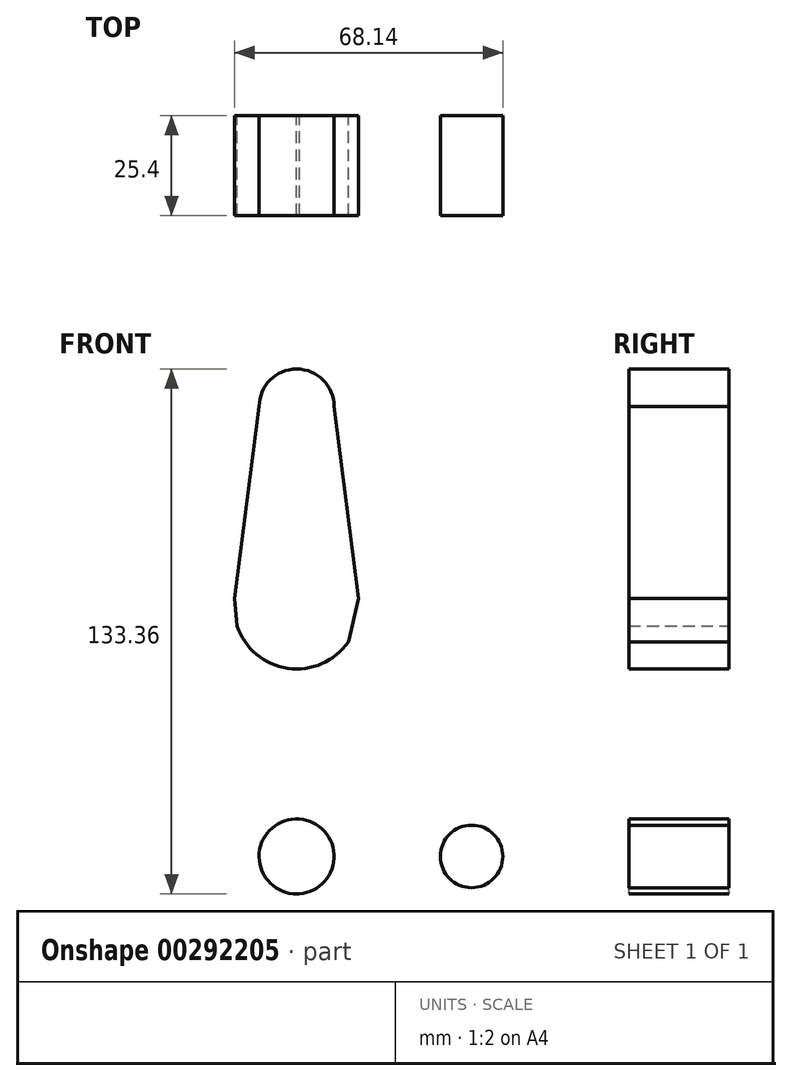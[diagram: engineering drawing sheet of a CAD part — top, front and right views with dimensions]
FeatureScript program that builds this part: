
annotation { "Feature Type Name" : "Feature", "Feature Type Description" : "" }
export const myFeature = defineFeature(function(context is Context, id is Id, definition is map)
    precondition{}
    {
        {
            var Q0;
            Q0=qCreatedBy(makeId("Front.planeOp"),FACE);
            var sketch = newSketch(context, id + "F0", { "sketchPlane" : qUnion([Q0])});
            skCircle(sketch, "E0", {"center": v(0, 114.3) * mm, "radius": 9.53 * mm});
            skCircle(sketch, "E1", {"center": v(0, 63.5) * mm, "radius": 15.88 * mm});
            skCircle(sketch, "E2", {"center": v(0, 0) * mm, "radius": 9.53 * mm});
            skCircle(sketch, "E3", {"center": v(44.45, 0) * mm, "radius": 7.94 * mm});
            skLineSegment(sketch, "E4", {"start": v(0, 114.3) * mm, "end": v(0, 79.38) * mm});
            skLineSegment(sketch, "E5", {"start": v(0, 0) * mm, "end": v(9.53, 0) * mm});
            skLineSegment(sketch, "E6.trimOffspring", {"start": v(0, 9.53) * mm, "end": v(0, 0) * mm});
            skPoint(sketch, "E7.start.orphan", {"position": v(-9.53, 114.3) * mm});
            skLineSegment(sketch, "E8", {"start": v(-9.53, 114.3) * mm, "end": v(-15.75, 65.5) * mm});
            skLineSegment(sketch, "E9", {"start": v(-15.75, 65.5) * mm, "end": v(-9.57, 0) * mm});
            skLineSegment(sketch, "E10.trimOffspring", {"start": v(36.51, 0) * mm, "end": v(44.45, 0) * mm});
            skLineSegment(sketch, "E11", {"start": v(18.97, 8.85) * mm, "end": v(44.73, 7.93) * mm});
            skLineSegment(sketch, "E12", {"start": v(0, -9.53) * mm, "end": v(44.73, -7.93) * mm});
            skPoint(sketch, "E13.end.orphan", {"position": v(234.08, -36.82) * mm});
            skArc(sketch, "E14.filletArc", {"start": v(11.34, 17.61) * mm, "mid": v(13.25, 11.58) * mm, "end": v(18.97, 8.85) * mm});
            skLineSegment(sketch, "E15", {"start": v(9.52, 114.3) * mm, "end": v(15.75, 65.5) * mm});
            skLineSegment(sketch, "E16", {"start": v(15.75, 65.5) * mm, "end": v(13.11, 54.55) * mm});
            skLineSegment(sketch, "E17", {"start": v(1.66, -0.4) * mm, "end": v(9.53, 0) * mm});
            skLineSegment(sketch, "E18.trimOffspring", {"start": v(2.23, 9.26) * mm, "end": v(0, 0) * mm});
            skLineSegment(sketch, "E19", {"start": v(13.11, 54.55) * mm, "end": v(11.34, 17.61) * mm});
            skSolve(sketch);
        }
        {
            var Q0;
            {var subQ0=sQuery(id+"F0.wireOp",EDGE,"52DSyJSs-urWb-Q2Su-mGJg-sDY8tmNg4yd1");var subQ1=sQuery(id+"F0.wireOp",EDGE,"E0");var subQ2=makeQuery(id+"F0.imprint","INTERSECT",VERTEX,{"derivedFrom":[subQ1,subQ0]});Q0=makeQuery(id+"F0.imprint","IMPRINT",FACE,{"disambiguationData":[TD([[makeQuery(id+"F0.imprint","IMPRINT",EDGE,{"disambiguationData":[TD([[subQ2,1.0]])],"derivedFrom":subQ1}),-1.0]])]});}
            var Q1;
            {var subQ0=sQuery(id+"F0.wireOp",EDGE,"E8");Q1=makeQuery(id+"F0.imprint","IMPRINT",FACE,{"disambiguationData":[TD([[makeQuery(id+"F0.imprint","IMPRINT",EDGE,{"derivedFrom":subQ0}),1.0]])]});}
            var Q2;
            {var subQ0=sQuery(id+"F0.wireOp",EDGE,"E0");var subQ1=makeQuery(id+"F0.imprint","INTERSECT",VERTEX,{"derivedFrom":[subQ0,sQuery(id+"F0.wireOp",EDGE,"E8")]});Q2=makeQuery(id+"F0.imprint","IMPRINT",FACE,{"disambiguationData":[TD([[makeQuery(id+"F0.imprint","IMPRINT",EDGE,{"disambiguationData":[TD([[subQ1,1.0]])],"derivedFrom":subQ0}),1.0]])]});}
            var Q3;
            {var subQ0=sQuery(id+"F0.wireOp",EDGE,"E1");var subQ1=makeQuery(id+"F0.imprint","INTERSECT",VERTEX,{"derivedFrom":[subQ0,sQuery(id+"F0.wireOp",EDGE,"E4")]});Q3=makeQuery(id+"F0.imprint","IMPRINT",FACE,{"disambiguationData":[TD([[makeQuery(id+"F0.imprint","IMPRINT",EDGE,{"disambiguationData":[TD([[subQ1,1.0]])],"derivedFrom":subQ0}),1.0]])]});}
            var Q4;
            {var subQ1=sQuery(id+"F0.wireOp",EDGE,"E5");Q4=makeQuery(id+"F0.imprint","IMPRINT",FACE,{"disambiguationData":[TD([[makeQuery(id+"F0.imprint","IMPRINT",EDGE,{"derivedFrom":subQ1}),-1.0]])]});}
            var Q5;
            {var subQ0=sQuery(id+"F0.wireOp",EDGE,"E3");var subQ1=makeQuery(id+"F0.imprint","IMPRINT",VERTEX,{"disambiguationData":[OD(0.0)],"derivedFrom":subQ0});Q5=makeQuery(id+"F0.imprint","IMPRINT",FACE,{"disambiguationData":[TD([[makeQuery(id+"F0.imprint","IMPRINT",EDGE,{"disambiguationData":[TD([[subQ1,1.0]])],"derivedFrom":subQ0}),1.0]])]});}
            var Q6;
            {var subQ0=sQuery(id+"F0.wireOp",EDGE,"E6.trimOffspring");Q6=makeQuery(id+"F0.imprint","IMPRINT",FACE,{"disambiguationData":[TD([[makeQuery(id+"F0.imprint","IMPRINT",EDGE,{"derivedFrom":subQ0}),1.0]])]});}
            var Q7;
            {var subQ0=sQuery(id+"F0.wireOp",EDGE,"E5");Q7=makeQuery(id+"F0.imprint","IMPRINT",FACE,{"disambiguationData":[TD([[makeQuery(id+"F0.imprint","IMPRINT",EDGE,{"derivedFrom":subQ0}),1.0]])]});}
            extrude(context, id + "F1", {"entities" : qUnion([Q0, Q1, Q2, Q3, Q4, Q5, Q6, Q7]), "depth" : 25.4 * mm});
        }
    });
